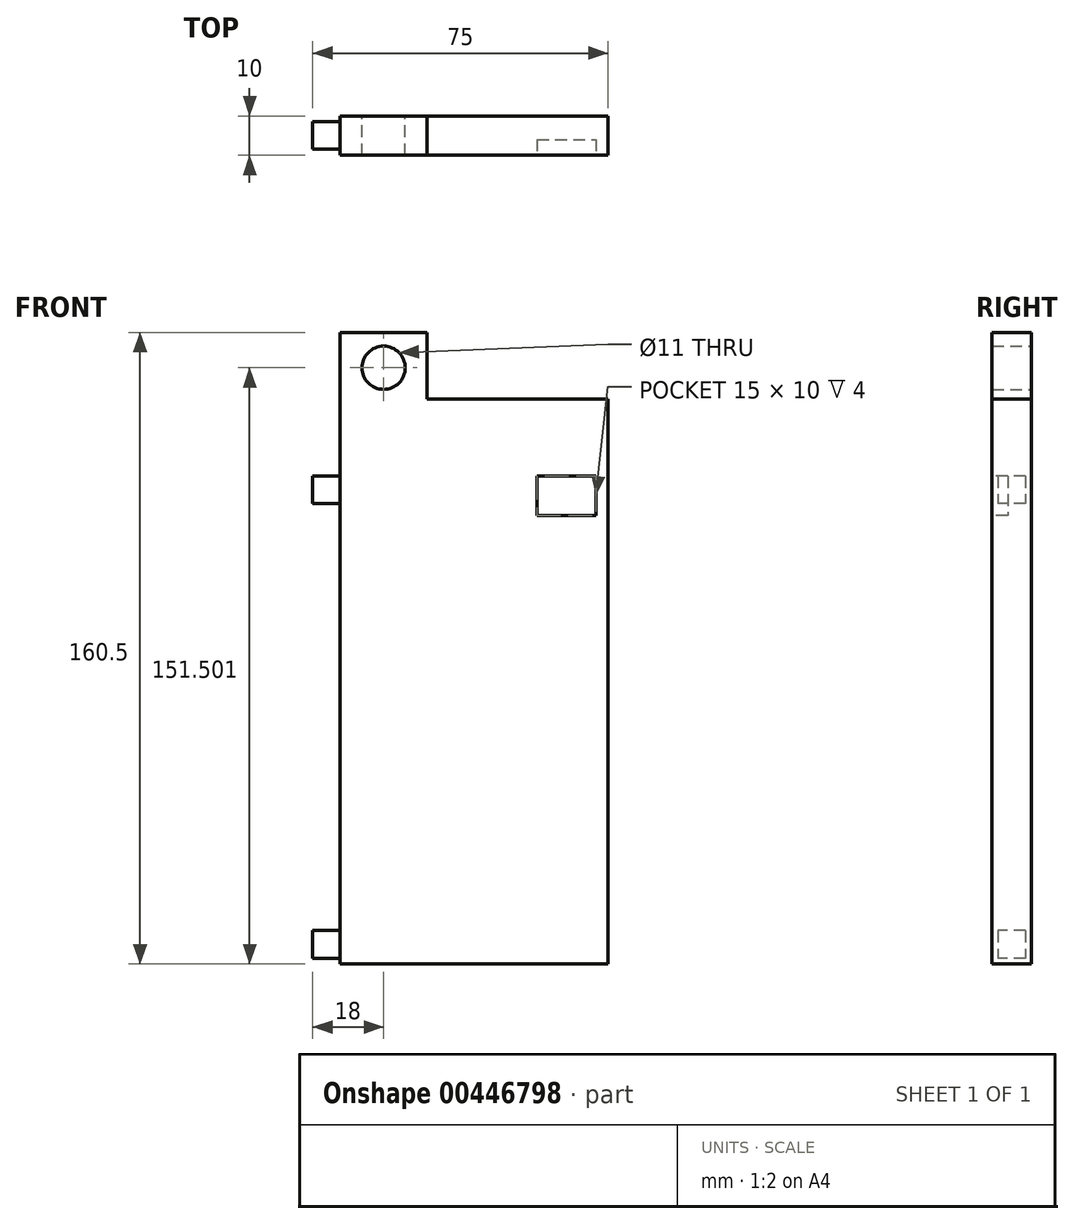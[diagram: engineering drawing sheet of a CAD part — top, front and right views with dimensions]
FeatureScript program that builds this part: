
annotation { "Feature Type Name" : "Feature", "Feature Type Description" : "" }
export const myFeature = defineFeature(function(context is Context, id is Id, definition is map)
    precondition{}
    {
        {
            var Q0;
            Q0=qCreatedBy(makeId("Front.planeOp"),FACE);
            var sketch = newSketch(context, id + "F0", { "sketchPlane" : qUnion([Q0])});
            skLineSegment(sketch, "E0", {"start": v(-183, -90.6) * mm, "end": v(183, -90.6) * mm});
            skLineSegment(sketch, "E1", {"start": v(183, -90.6) * mm, "end": v(183, 64.4) * mm});
            skLineSegment(sketch, "E2", {"start": v(183, 64.4) * mm, "end": v(115, 64.4) * mm});
            skLineSegment(sketch, "E3", {"start": v(115, 64.4) * mm, "end": v(115, 49.4) * mm});
            skLineSegment(sketch, "E4", {"start": v(115, 49.4) * mm, "end": v(-115, 49.4) * mm});
            skLineSegment(sketch, "E5", {"start": v(-115, 49.4) * mm, "end": v(-115, 64.4) * mm});
            skLineSegment(sketch, "E6", {"start": v(-115, 64.4) * mm, "end": v(-183, 64.4) * mm});
            skLineSegment(sketch, "E7", {"start": v(-183, 64.4) * mm, "end": v(-183, -90.6) * mm});
            skSolve(sketch);
        }
        {
            var Q0;
            Q0=qSketchRegion(id+"F0",true);
            extrude(context, id + "F1", {"entities" : qUnion([Q0]), "depth" : 10 * mm});
        }
        {
            var Q0;
            Q0=makeQuery(id+"F1.opExtrude","CAP_FACE",FACE,{"disambiguationData":[OSD([sQuery(id+"F0.wireOp",EDGE,"E0"),sQuery(id+"F0.wireOp",EDGE,"E1"),sQuery(id+"F0.wireOp",EDGE,"E2"),sQuery(id+"F0.wireOp",EDGE,"E3"),sQuery(id+"F0.wireOp",EDGE,"E4"),sQuery(id+"F0.wireOp",EDGE,"E5"),sQuery(id+"F0.wireOp",EDGE,"E6"),sQuery(id+"F0.wireOp",EDGE,"E7"),sQuery(id+"F0.wireOp",EDGE,"uUBPHAbE-gvHs-FxYo-3iu7-rJtuFPwepcCj.bottom"),sQuery(id+"F0.wireOp",EDGE,"uUBPHAbE-gvHs-FxYo-3iu7-rJtuFPwepcCj.top"),sQuery(id+"F0.wireOp",EDGE,"uUBPHAbE-gvHs-FxYo-3iu7-rJtuFPwepcCj.left"),sQuery(id+"F0.wireOp",EDGE,"uUBPHAbE-gvHs-FxYo-3iu7-rJtuFPwepcCj.right")])],"isStart":true});
            var sketch = newSketch(context, id + "F2", { "sketchPlane" : qUnion([Q0])});
            skLineSegment(sketch, "E8.bottom", {"start": v(-183, 64.4) * mm, "end": v(-137, 64.4) * mm});
            skLineSegment(sketch, "E8.top", {"start": v(-183, 49.4) * mm, "end": v(-137, 49.4) * mm});
            skLineSegment(sketch, "E8.left", {"start": v(-183, 64.4) * mm, "end": v(-183, 49.4) * mm});
            skLineSegment(sketch, "E8.right", {"start": v(-137, 64.4) * mm, "end": v(-137, 49.4) * mm});
            skLineSegment(sketch, "E9.bottom", {"start": v(183, 64.4) * mm, "end": v(137, 64.4) * mm});
            skLineSegment(sketch, "E9.top", {"start": v(183, 49.4) * mm, "end": v(137, 49.4) * mm});
            skLineSegment(sketch, "E9.left", {"start": v(183, 64.4) * mm, "end": v(183, 49.4) * mm});
            skLineSegment(sketch, "E9.right", {"start": v(137, 64.4) * mm, "end": v(137, 49.4) * mm});
            skSolve(sketch);
        }
        {
            var Q0;
            Q0=makeQuery(id+"F2.imprint","IMPRINT",FACE,{"disambiguationData":[TD([[makeQuery(id+"F2.imprint","IMPRINT",EDGE,{"derivedFrom":sQuery(id+"F2.wireOp",EDGE,"E8.bottom")}),-1.0]])]});
            var Q1;
            Q1=makeQuery(id+"F2.imprint","IMPRINT",FACE,{"disambiguationData":[TD([[makeQuery(id+"F2.imprint","IMPRINT",EDGE,{"derivedFrom":sQuery(id+"F2.wireOp",EDGE,"E9.bottom")}),-1.0]])]});
            extrude(context, id + "F3", {"entities" : qUnion([Q0, Q1]), "operationType" : NewBodyOperationType.REMOVE, "oppositeDirection" : true, "depth" : 25 * mm});
        }
        {
            var Q0;
            Q0=makeQuery(id+"F1.opExtrude","CAP_FACE",FACE,{"disambiguationData":[OSD([sQuery(id+"F0.wireOp",EDGE,"E0"),sQuery(id+"F0.wireOp",EDGE,"E1"),sQuery(id+"F0.wireOp",EDGE,"E2"),sQuery(id+"F0.wireOp",EDGE,"E3"),sQuery(id+"F0.wireOp",EDGE,"E4"),sQuery(id+"F0.wireOp",EDGE,"E5"),sQuery(id+"F0.wireOp",EDGE,"E6"),sQuery(id+"F0.wireOp",EDGE,"E7")])],"isStart":true});
            var sketch = newSketch(context, id + "F4", { "sketchPlane" : qUnion([Q0])});
            skLineSegment(sketch, "E10.bottom", {"start": v(183, 33.4) * mm, "end": v(-183, 33.4) * mm});
            skLineSegment(sketch, "E10.top", {"start": v(183, 23.4) * mm, "end": v(-183, 23.4) * mm});
            skLineSegment(sketch, "E10.left", {"start": v(183, 33.4) * mm, "end": v(183, 23.4) * mm});
            skLineSegment(sketch, "E10.right", {"start": v(-183, 33.4) * mm, "end": v(-183, 23.4) * mm});
            skSolve(sketch);
        }
        {
            var Q0;
            Q0=makeQuery(id+"F4.imprint","IMPRINT",FACE,{"disambiguationData":[TD([[makeQuery(id+"F4.imprint","IMPRINT",EDGE,{"derivedFrom":sQuery(id+"F4.wireOp",EDGE,"E10.bottom")}),1.0]])]});
            extrude(context, id + "F5", {"entities" : qUnion([Q0]), "operationType" : NewBodyOperationType.ADD, "depth" : 40 * mm});
        }
        {
            var Q0;
            {var subQ0=sQuery(id+"F0.wireOp",EDGE,"E7");var subQ1=sQuery(id+"F0.wireOp",EDGE,"E1");var subQ2=sQuery(id+"F0.wireOp",EDGE,"E0");Q0=makeQuery(id+"F5.boolean.opBoolean","SPLIT",FACE,{"disambiguationData":[TD([makeQuery(id+"F1.opExtrude","SWEPT_FACE",FACE,{"disambiguationData":[OSD([subQ2])]})])],"derivedFrom":makeQuery(id+"F1.opExtrude","CAP_FACE",FACE,{"disambiguationData":[OSD([subQ2,subQ1,sQuery(id+"F0.wireOp",EDGE,"E2"),sQuery(id+"F0.wireOp",EDGE,"E3"),sQuery(id+"F0.wireOp",EDGE,"E4"),sQuery(id+"F0.wireOp",EDGE,"E5"),sQuery(id+"F0.wireOp",EDGE,"E6"),subQ0])],"isStart":true})});}
            var sketch = newSketch(context, id + "F6", { "sketchPlane" : qUnion([Q0])});
            skLineSegment(sketch, "E11.bottom", {"start": v(-115, -75.6) * mm, "end": v(115, -75.6) * mm});
            skLineSegment(sketch, "E11.top", {"start": v(-115, 23.4) * mm, "end": v(115, 23.4) * mm});
            skLineSegment(sketch, "E11.left", {"start": v(-115, -75.6) * mm, "end": v(-115, 23.4) * mm});
            skLineSegment(sketch, "E11.right", {"start": v(115, -75.6) * mm, "end": v(115, 23.4) * mm});
            skSolve(sketch);
        }
        {
            var Q0;
            Q0=makeQuery(id+"F6.imprint","IMPRINT",FACE,{"disambiguationData":[TD([[makeQuery(id+"F6.imprint","IMPRINT",EDGE,{"derivedFrom":sQuery(id+"F6.wireOp",EDGE,"E11.bottom")}),1.0]])]});
            extrude(context, id + "F7", {"entities" : qUnion([Q0]), "operationType" : NewBodyOperationType.REMOVE, "oppositeDirection" : true, "depth" : 25 * mm});
        }
        {
            var Q0;
            {var subQ0=sQuery(id+"F0.wireOp",EDGE,"E7");var subQ1=sQuery(id+"F0.wireOp",EDGE,"E6");var subQ2=sQuery(id+"F0.wireOp",EDGE,"E5");var subQ3=sQuery(id+"F0.wireOp",EDGE,"E1");var subQ4=sQuery(id+"F0.wireOp",EDGE,"E2");var subQ5=sQuery(id+"F0.wireOp",EDGE,"E3");var subQ6=sQuery(id+"F0.wireOp",EDGE,"E4");Q0=makeQuery(id+"F5.boolean.opBoolean","SPLIT",FACE,{"disambiguationData":[TD([makeQuery(id+"F1.opExtrude","SWEPT_FACE",FACE,{"disambiguationData":[OSD([subQ4])]})])],"derivedFrom":makeQuery(id+"F1.opExtrude","CAP_FACE",FACE,{"disambiguationData":[OSD([sQuery(id+"F0.wireOp",EDGE,"E0"),subQ3,subQ4,subQ5,subQ6,subQ2,subQ1,subQ0])],"isStart":true})});}
            var sketch = newSketch(context, id + "F8", { "sketchPlane" : qUnion([Q0])});
            skLineSegment(sketch, "E12.bottom", {"start": v(-115, 49.4) * mm, "end": v(115, 49.4) * mm});
            skLineSegment(sketch, "E12.top", {"start": v(-115, 33.4) * mm, "end": v(115, 33.4) * mm});
            skLineSegment(sketch, "E12.left", {"start": v(-115, 49.4) * mm, "end": v(-115, 33.4) * mm});
            skLineSegment(sketch, "E12.right", {"start": v(115, 49.4) * mm, "end": v(115, 33.4) * mm});
            skSolve(sketch);
        }
        {
            var Q0;
            Q0=makeQuery(id+"F8.imprint","IMPRINT",FACE,{"disambiguationData":[TD([[makeQuery(id+"F8.imprint","IMPRINT",EDGE,{"derivedFrom":sQuery(id+"F8.wireOp",EDGE,"E12.bottom")}),-1.0]])]});
            extrude(context, id + "F9", {"entities" : qUnion([Q0]), "operationType" : NewBodyOperationType.REMOVE, "oppositeDirection" : true, "depth" : 25 * mm});
        }
        {
            var Q0;
            {var subQ1=sQuery(id+"F0.wireOp",EDGE,"E5");var subQ2=makeQuery(id+"F1.opExtrude","SWEPT_FACE",FACE,{"disambiguationData":[OSD([subQ1])]});var subQ3=sQuery(id+"F0.wireOp",EDGE,"E7");var subQ5=sQuery(id+"F0.wireOp",EDGE,"E6");var subQ10=sQuery(id+"F0.wireOp",EDGE,"E1");var subQ11=sQuery(id+"F0.wireOp",EDGE,"E2");var subQ12=sQuery(id+"F0.wireOp",EDGE,"E3");var subQ13=sQuery(id+"F0.wireOp",EDGE,"E4");Q0=makeQuery(id+"F9.boolean.opBoolean","SPLIT",FACE,{"disambiguationData":[TD([subQ2])],"derivedFrom":makeQuery(id+"F5.boolean.opBoolean","SPLIT",FACE,{"disambiguationData":[TD([makeQuery(id+"F1.opExtrude","SWEPT_FACE",FACE,{"disambiguationData":[OSD([subQ11])]})])],"derivedFrom":makeQuery(id+"F1.opExtrude","CAP_FACE",FACE,{"disambiguationData":[OSD([sQuery(id+"F0.wireOp",EDGE,"E0"),subQ10,subQ11,subQ12,subQ13,subQ1,subQ5,subQ3])],"isStart":true})})});}
            var sketch = newSketch(context, id + "F10", { "sketchPlane" : qUnion([Q0])});
            skCircle(sketch, "E13", {"center": v(125, 57.4) * mm, "radius": 5.5 * mm});
            skSolve(sketch);
        }
        {
            var Q0;
            Q0=makeQuery(id+"F10.imprint","IMPRINT",FACE,{"disambiguationData":[TD([[makeQuery(id+"F10.imprint","IMPRINT",EDGE,{"derivedFrom":sQuery(id+"F10.wireOp",EDGE,"E13")}),1.0]])]});
            extrude(context, id + "F11", {"entities" : qUnion([Q0]), "operationType" : NewBodyOperationType.REMOVE, "oppositeDirection" : true, "depth" : 25 * mm});
        }
        {
            var Q0;
            Q0=makeQuery(id+"F5.boolean.opBoolean","MERGE",FACE,{"derivedFrom":[makeQuery(id+"F1.opExtrude","SWEPT_FACE",FACE,{"disambiguationData":[OSD([sQuery(id+"F0.wireOp",EDGE,"E1")])]}),makeQuery(id+"F5.opExtrude","SWEPT_FACE",FACE,{"disambiguationData":[OSD([sQuery(id+"F4.wireOp",EDGE,"E10.right")])]})]});
            var sketch = newSketch(context, id + "F12", { "sketchPlane" : qUnion([Q0])});
            skLineSegment(sketch, "E14.bottom", {"start": v(40, 33.4) * mm, "end": v(0, 33.4) * mm});
            skLineSegment(sketch, "E14.top", {"start": v(40, 23.4) * mm, "end": v(0, 23.4) * mm});
            skLineSegment(sketch, "E14.left", {"start": v(40, 33.4) * mm, "end": v(40, 23.4) * mm});
            skLineSegment(sketch, "E14.right", {"start": v(0, 33.4) * mm, "end": v(0, 23.4) * mm});
            skSolve(sketch);
        }
        {
            var Q0;
            Q0=makeQuery(id+"F12.imprint","IMPRINT",FACE,{"disambiguationData":[TD([[makeQuery(id+"F12.imprint","IMPRINT",EDGE,{"derivedFrom":sQuery(id+"F12.wireOp",EDGE,"E14.bottom")}),1.0]])]});
            extrude(context, id + "F13", {"entities" : qUnion([Q0]), "operationType" : NewBodyOperationType.REMOVE, "endBound" : BoundingType.UP_TO_NEXT, "oppositeDirection" : true, "depth" : 25 * mm});
        }
        {
            var Q0;
            {var subQ1=sQuery(id+"F0.wireOp",EDGE,"E5");var subQ2=makeQuery(id+"F1.opExtrude","SWEPT_FACE",FACE,{"disambiguationData":[OSD([subQ1])]});var subQ3=sQuery(id+"F0.wireOp",EDGE,"E7");var subQ5=sQuery(id+"F0.wireOp",EDGE,"E6");var subQ11=sQuery(id+"F0.wireOp",EDGE,"E1");var subQ12=makeQuery(id+"F1.opExtrude","SWEPT_FACE",FACE,{"disambiguationData":[OSD([subQ11])]});var subQ13=sQuery(id+"F0.wireOp",EDGE,"E2");var subQ14=makeQuery(id+"F1.opExtrude","SWEPT_FACE",FACE,{"disambiguationData":[OSD([subQ13])]});var subQ16=sQuery(id+"F0.wireOp",EDGE,"E3");var subQ19=sQuery(id+"F0.wireOp",EDGE,"E4");var subQ21=sQuery(id+"F0.wireOp",EDGE,"E0");var subQ22=makeQuery(id+"F1.opExtrude","CAP_FACE",FACE,{"disambiguationData":[OSD([subQ21,subQ11,subQ13,subQ16,subQ19,subQ1,subQ5,subQ3])],"isStart":true});var subQ23=makeQuery(id+"F5.boolean.opBoolean","SPLIT",FACE,{"disambiguationData":[TD([subQ14])],"derivedFrom":subQ22});Q0=makeQuery(id+"F13.boolean.opBoolean","MERGE",FACE,{"derivedFrom":[makeQuery(id+"F5.boolean.opBoolean","SPLIT",FACE,{"disambiguationData":[TD([makeQuery(id+"F1.opExtrude","SWEPT_FACE",FACE,{"disambiguationData":[OSD([subQ21])]})])],"derivedFrom":subQ22}),makeQuery(id+"F9.boolean.opBoolean","SPLIT",FACE,{"disambiguationData":[TD([subQ12])],"derivedFrom":subQ23}),makeQuery(id+"F9.boolean.opBoolean","SPLIT",FACE,{"disambiguationData":[TD([subQ2])],"derivedFrom":subQ23})],"fromTools":[makeQuery(id+"F13.opExtrude","SWEPT_FACE",FACE,{"disambiguationData":[OSD([sQuery(id+"F12.wireOp",EDGE,"E14.right")])]})]});}
            var sketch = newSketch(context, id + "F14", { "sketchPlane" : qUnion([Q0])});
            skPoint(sketch, "E15.firstSnap0", {"position": v(160, 49.4) * mm});
            skLineSegment(sketch, "E16.bottom", {"start": v(165, 33.4) * mm, "end": v(180, 33.4) * mm});
            skLineSegment(sketch, "E16.top", {"start": v(165, 23.4) * mm, "end": v(180, 23.4) * mm});
            skLineSegment(sketch, "E16.left", {"start": v(165, 33.4) * mm, "end": v(165, 23.4) * mm});
            skLineSegment(sketch, "E16.right", {"start": v(180, 33.4) * mm, "end": v(180, 23.4) * mm});
            skSolve(sketch);
        }
        {
            var Q0;
            Q0=qSketchRegion(id+"F14",true);
            extrude(context, id + "F15", {"entities" : qUnion([Q0]), "operationType" : NewBodyOperationType.REMOVE, "oppositeDirection" : true, "depth" : 4 * mm});
        }
        {
            var Q0;
            Q0=makeQuery(id+"F9.boolean.opBoolean","MERGE",FACE,{"derivedFrom":[makeQuery(id+"F1.opExtrude","SWEPT_FACE",FACE,{"disambiguationData":[OSD([sQuery(id+"F0.wireOp",EDGE,"E3")])]}),makeQuery(id+"F9.opExtrude","SWEPT_FACE",FACE,{"disambiguationData":[OSD([sQuery(id+"F8.wireOp",EDGE,"E12.left")])]})]});
            var sketch = newSketch(context, id + "F16", { "sketchPlane" : qUnion([Q0])});
            skLineSegment(sketch, "E17.bottom", {"start": v(-46.86, 79.62) * mm, "end": v(50.61, 79.62) * mm});
            skLineSegment(sketch, "E17.top", {"start": v(-46.86, -108.49) * mm, "end": v(50.61, -108.49) * mm});
            skLineSegment(sketch, "E17.left", {"start": v(-46.86, 79.62) * mm, "end": v(-46.86, -108.49) * mm});
            skLineSegment(sketch, "E17.right", {"start": v(50.61, 79.62) * mm, "end": v(50.61, -108.49) * mm});
            skSolve(sketch);
        }
        {
            var Q0;
            Q0=qSketchRegion(id+"F16",true);
            extrude(context, id + "F17", {"entities" : qUnion([Q0]), "operationType" : NewBodyOperationType.REMOVE, "depth" : 300 * mm});
        }
        {
            var Q0;
            Q0=makeQuery(id+"F17.boolean.opBoolean","MERGE",FACE,{"derivedFrom":[makeQuery(id+"F7.boolean.opBoolean","COPY",FACE,{"derivedFrom":makeQuery(id+"F7.opExtrude","SWEPT_FACE",FACE,{"disambiguationData":[OSD([sQuery(id+"F6.wireOp",EDGE,"E11.left")])]})}),makeQuery(id+"F9.boolean.opBoolean","MERGE",FACE,{"derivedFrom":[makeQuery(id+"F1.opExtrude","SWEPT_FACE",FACE,{"disambiguationData":[OSD([sQuery(id+"F0.wireOp",EDGE,"E3")])]}),makeQuery(id+"F9.opExtrude","SWEPT_FACE",FACE,{"disambiguationData":[OSD([sQuery(id+"F8.wireOp",EDGE,"E12.left")])]})]}),makeQuery(id+"F17.opExtrude","CAP_FACE",FACE,{"disambiguationData":[OSD([sQuery(id+"F16.wireOp",EDGE,"E17.bottom"),sQuery(id+"F16.wireOp",EDGE,"E17.top"),sQuery(id+"F16.wireOp",EDGE,"E17.left"),sQuery(id+"F16.wireOp",EDGE,"E17.right")])],"isStart":true})]});
            var sketch = newSketch(context, id + "F18", { "sketchPlane" : qUnion([Q0])});
            skLineSegment(sketch, "E18.bottom", {"start": v(1.5, -82.1) * mm, "end": v(8.5, -82.1) * mm});
            skLineSegment(sketch, "E18.top", {"start": v(1.5, -89.1) * mm, "end": v(8.5, -89.1) * mm});
            skLineSegment(sketch, "E18.left", {"start": v(1.5, -82.1) * mm, "end": v(1.5, -89.1) * mm});
            skLineSegment(sketch, "E18.right", {"start": v(8.5, -82.1) * mm, "end": v(8.5, -89.1) * mm});
            skLineSegment(sketch, "E19.bottom", {"start": v(1.5, 33.4) * mm, "end": v(8.5, 33.4) * mm});
            skLineSegment(sketch, "E19.top", {"start": v(1.5, 26.4) * mm, "end": v(8.5, 26.4) * mm});
            skLineSegment(sketch, "E19.left", {"start": v(1.5, 33.4) * mm, "end": v(1.5, 26.4) * mm});
            skLineSegment(sketch, "E19.right", {"start": v(8.5, 33.4) * mm, "end": v(8.5, 26.4) * mm});
            skSolve(sketch);
        }
        {
            var Q0;
            Q0=qSketchRegion(id+"F18",true);
            extrude(context, id + "F19", {"entities" : qUnion([Q0]), "operationType" : NewBodyOperationType.ADD, "depth" : 7 * mm});
        }
        {
            var Q0;
            Q0=makeQuery(id+"F1.opExtrude","CAP_FACE",FACE,{"disambiguationData":[OSD([sQuery(id+"F0.wireOp",EDGE,"E0"),sQuery(id+"F0.wireOp",EDGE,"E1"),sQuery(id+"F0.wireOp",EDGE,"E2"),sQuery(id+"F0.wireOp",EDGE,"E3"),sQuery(id+"F0.wireOp",EDGE,"E4"),sQuery(id+"F0.wireOp",EDGE,"E5"),sQuery(id+"F0.wireOp",EDGE,"E6"),sQuery(id+"F0.wireOp",EDGE,"E7")])],"isStart":false});
            var sketch = newSketch(context, id + "F20", { "sketchPlane" : qUnion([Q0])});
            skLineSegment(sketch, "E20.0.0", {"start": v(180, 33.4) * mm, "end": v(180, 23.4) * mm});
            skLineSegment(sketch, "E20.0.1", {"start": v(180, 23.4) * mm, "end": v(165, 23.4) * mm});
            skLineSegment(sketch, "E20.0.2", {"start": v(165, 23.4) * mm, "end": v(165, 33.4) * mm});
            skLineSegment(sketch, "E20.0.3", {"start": v(165, 33.4) * mm, "end": v(180, 33.4) * mm});
            skSolve(sketch);
        }
        {
            var Q0;
            Q0=qSketchRegion(id+"F20",true);
            extrude(context, id + "F21", {"entities" : qUnion([Q0]), "operationType" : NewBodyOperationType.REMOVE, "oppositeDirection" : true, "depth" : 4 * mm});
        }
        {
            var Q0;
            Q0=makeQuery(id+"F3.boolean.opBoolean","COPY",FACE,{"derivedFrom":makeQuery(id+"F3.opExtrude","SWEPT_FACE",FACE,{"disambiguationData":[OSD([sQuery(id+"F2.wireOp",EDGE,"E8.top")])]})});
            extrude(context, id + "F22", {"entities" : qUnion([Q0]), "operationType" : NewBodyOperationType.ADD, "depth" : 3.5 * mm});
        }
        {
            var Q0;
            Q0=makeQuery(id+"F1.opExtrude","SWEPT_FACE",FACE,{"disambiguationData":[OSD([sQuery(id+"F0.wireOp",EDGE,"E2")])]});
            extrude(context, id + "F23", {"entities" : qUnion([Q0]), "operationType" : NewBodyOperationType.ADD, "depth" : 1.5 * mm});
        }
        {
            var Q0;
            Q0=makeQuery(id+"F23.opExtrude","CAP_FACE",FACE,{"disambiguationData":[OSD([sQuery(id+"F0.wireOp",EDGE,"E2")])],"isStart":false});
            extrude(context, id + "F24", {"entities" : qUnion([Q0]), "operationType" : NewBodyOperationType.ADD, "depth" : 4 * mm});
        }
        {
            var Q0;
            {var subQ0=sQuery(id+"F0.wireOp",EDGE,"E2");var subQ1=makeQuery(id+"F1.opExtrude","CAP_EDGE",EDGE,{"disambiguationData":[OSD([subQ0])],"isStart":true});var subQ2=sQuery(id+"F2.wireOp",EDGE,"E8.top");var subQ4=sQuery(id+"F0.wireOp",EDGE,"E5");var subQ5=makeQuery(id+"F1.opExtrude","SWEPT_FACE",FACE,{"disambiguationData":[OSD([subQ4])]});var subQ6=sQuery(id+"F0.wireOp",EDGE,"E7");var subQ8=sQuery(id+"F0.wireOp",EDGE,"E6");var subQ14=sQuery(id+"F0.wireOp",EDGE,"E1");var subQ15=makeQuery(id+"F1.opExtrude","SWEPT_FACE",FACE,{"disambiguationData":[OSD([subQ14])]});var subQ16=makeQuery(id+"F1.opExtrude","SWEPT_FACE",FACE,{"disambiguationData":[OSD([subQ0])]});var subQ18=sQuery(id+"F0.wireOp",EDGE,"E3");var subQ21=sQuery(id+"F0.wireOp",EDGE,"E4");var subQ23=sQuery(id+"F0.wireOp",EDGE,"E0");var subQ24=makeQuery(id+"F1.opExtrude","CAP_FACE",FACE,{"disambiguationData":[OSD([subQ23,subQ14,subQ0,subQ18,subQ21,subQ4,subQ8,subQ6])],"isStart":true});var subQ25=makeQuery(id+"F5.boolean.opBoolean","SPLIT",FACE,{"disambiguationData":[TD([subQ16])],"derivedFrom":subQ24});Q0=makeQuery(id+"F24.boolean.opBoolean","MERGE",FACE,{"derivedFrom":[makeQuery(id+"F23.boolean.opBoolean","MERGE",FACE,{"derivedFrom":[makeQuery(id+"F22.boolean.opBoolean","MERGE",FACE,{"derivedFrom":[makeQuery(id+"F13.boolean.opBoolean","MERGE",FACE,{"derivedFrom":[makeQuery(id+"F5.boolean.opBoolean","SPLIT",FACE,{"disambiguationData":[TD([makeQuery(id+"F1.opExtrude","SWEPT_FACE",FACE,{"disambiguationData":[OSD([subQ23])]})])],"derivedFrom":subQ24}),makeQuery(id+"F9.boolean.opBoolean","SPLIT",FACE,{"disambiguationData":[TD([subQ15])],"derivedFrom":subQ25}),makeQuery(id+"F9.boolean.opBoolean","SPLIT",FACE,{"disambiguationData":[TD([subQ5])],"derivedFrom":subQ25})],"fromTools":[makeQuery(id+"F13.opExtrude","SWEPT_FACE",FACE,{"disambiguationData":[OSD([sQuery(id+"F12.wireOp",EDGE,"E14.right")])]})]}),makeQuery(id+"F22.opExtrude","SWEPT_FACE",FACE,{"disambiguationData":[OSD([subQ2])]})]}),makeQuery(id+"F23.opExtrude","SWEPT_FACE",FACE,{"disambiguationData":[OSD([subQ0]),TDD([subQ1])]})]}),makeQuery(id+"F24.opExtrude","SWEPT_FACE",FACE,{"disambiguationData":[OSD([subQ0]),TDD([makeQuery(id+"F23.opExtrude","CAP_EDGE",EDGE,{"disambiguationData":[OSD([subQ0]),TDD([subQ1])],"isStart":false})])]})]});}
            var sketch = newSketch(context, id + "F25", { "sketchPlane" : qUnion([Q0])});
            skLineSegment(sketch, "E21.0.0", {"start": v(-183, -90.6) * mm, "end": v(-115, -90.6) * mm});
            skLineSegment(sketch, "E21.0.1", {"start": v(-115, -90.6) * mm, "end": v(-115, 69.9) * mm});
            skLineSegment(sketch, "E21.0.2", {"start": v(-115, 69.9) * mm, "end": v(-137, 69.9) * mm});
            skLineSegment(sketch, "E21.0.3", {"start": v(-137, 69.9) * mm, "end": v(-137, 52.9) * mm});
            skLineSegment(sketch, "E21.0.4", {"start": v(-137, 52.9) * mm, "end": v(-183, 52.9) * mm});
            skLineSegment(sketch, "E21.0.5", {"start": v(-183, 52.9) * mm, "end": v(-183, -90.6) * mm});
            skCircle(sketch, "E22", {"center": v(-126, 60.9) * mm, "radius": 5.5 * mm});
            skSolve(sketch);
        }
        {
            var Q0;
            Q0=makeQuery(id+"F25.imprint","IMPRINT",FACE,{"disambiguationData":[TD([[makeQuery(id+"F25.imprint","IMPRINT",EDGE,{"derivedFrom":sQuery(id+"F25.wireOp",EDGE,"E22")}),1.0]])]});
            extrude(context, id + "F26", {"entities" : qUnion([Q0]), "operationType" : NewBodyOperationType.REMOVE, "oppositeDirection" : true, "depth" : 25 * mm});
        }
    });
